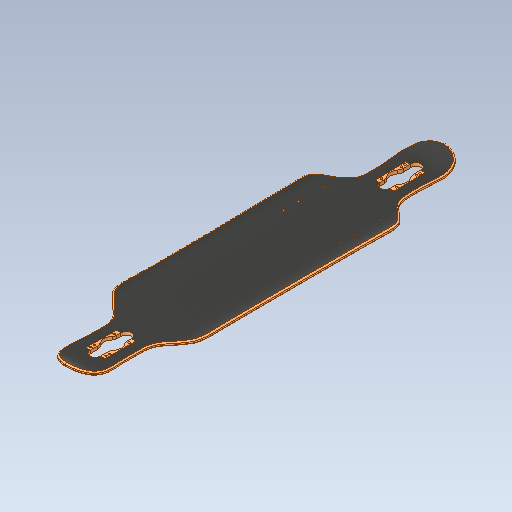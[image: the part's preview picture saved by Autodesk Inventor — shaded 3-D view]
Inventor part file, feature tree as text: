
AUTODESK INVENTOR PART (.ipt)
format: ipt  version: 2020.1 (Build 241239000, 239)  size: 6,171,648 bytes
history: native  units: in
note: dims shown in document units (in); Inventor stores cm internally (conversion verified against a paired STEP export)
features: other x8, sketch x6, extrude x6, plane x2, loft x1, fillet x1
ambient origin geometry x8: Origin, YZ Plane, XZ Plane, XY Plane, X Axis, Y Axis, Z Axis, Center Point
bodies: Body1 (feature_tree)
feature tree (24):
  sketch  "Sketch1"  dims[d113=9.6457in d114=40.748in]
  sketch  "Sketch2"  dims[d154=3.937in d155=40.748in d180=4.8228in]
  sketch  "Sketch3"  dims[d181=3.937in d183=9.6457in]
  other  "Bottom Profile"
  other  "Front Profile"
  other  "Front Profile Projection Plane"
  other  "Front Profile Projection"
  other  "Side Profile"
  loft  "Board Loft"
  extrude  "Shape Extrusion"  Depth=40.748in
  fillet  "Fillet6"  Radius=4.8228in
  plane  "Work Plane11"
  sketch  "Sketch26"  dims[d354=0.2165in d355=0.2165in]
  extrude  "Extrusion15"  Depth=9.6457in
  extrude  "Extrusion17"  Depth=0.2165in
  plane  "Work Plane12"
  sketch  "Sketch27"  dims[d356=20.374in d357=20.374in d378=2.126in d379=2.5in d384=0.9843in d394=0.5512in d395=180.0deg d396=0.5512in d397=180.0deg d400=0.7874in d401=0.3937in d402=3.3071in d403=0.7874in d404=0.5118in d408=5.9055in d409=0.0984in d410=0.0984in d412=90.0deg d413=5.9055in d414=0.3937in d415=0.3937in d417=0.3937in d421=0.3937in d545=1.2992in d546=0.2165in d547=1.6535in d548=3.0472in d549=0.7874in d551=2.7559in d552=0.3937in d554=0.3937in d556=0.7874in d558=1.5748in d559=0.3937in d561=0.3937in d563=2.0079in d564=0.0in d577=0.0055in d578=3.7205in d579=0.0055in d580=3.7205in d582=3.2087in d583=3.2087in d584=4.0197in d585=4.0197in d586=3.1969in d587=3.1969in d588=0.0in d589=0.0in d596=0.0in d597=90.0deg d598=0.0in d599=90.0deg d600=0.0in d601=90.0deg d602=14.4454in d603=0.0in d606=0.4724in d607=0.4724in d608=0.0039in d609=0.0in d610=0.4724in d612=0.4724in d613=0.0039in d614=0.0in d615=0.0039in d616=0.0in d617=0.0039in d618=0.0in d619=0.0787in d620=0.1181in]
  extrude  "Extrusion16"  Depth=0.2165in
  extrude  "Extrusion18"  Depth=0.3937in
  extrude  "Extrusion12"  Depth=0.3937in
  other  "Image4"
  other  "Image5"
  other  "Image6"
  sketch  "Sketch25"  dims[d350=0.813in d353=0.2165in]
